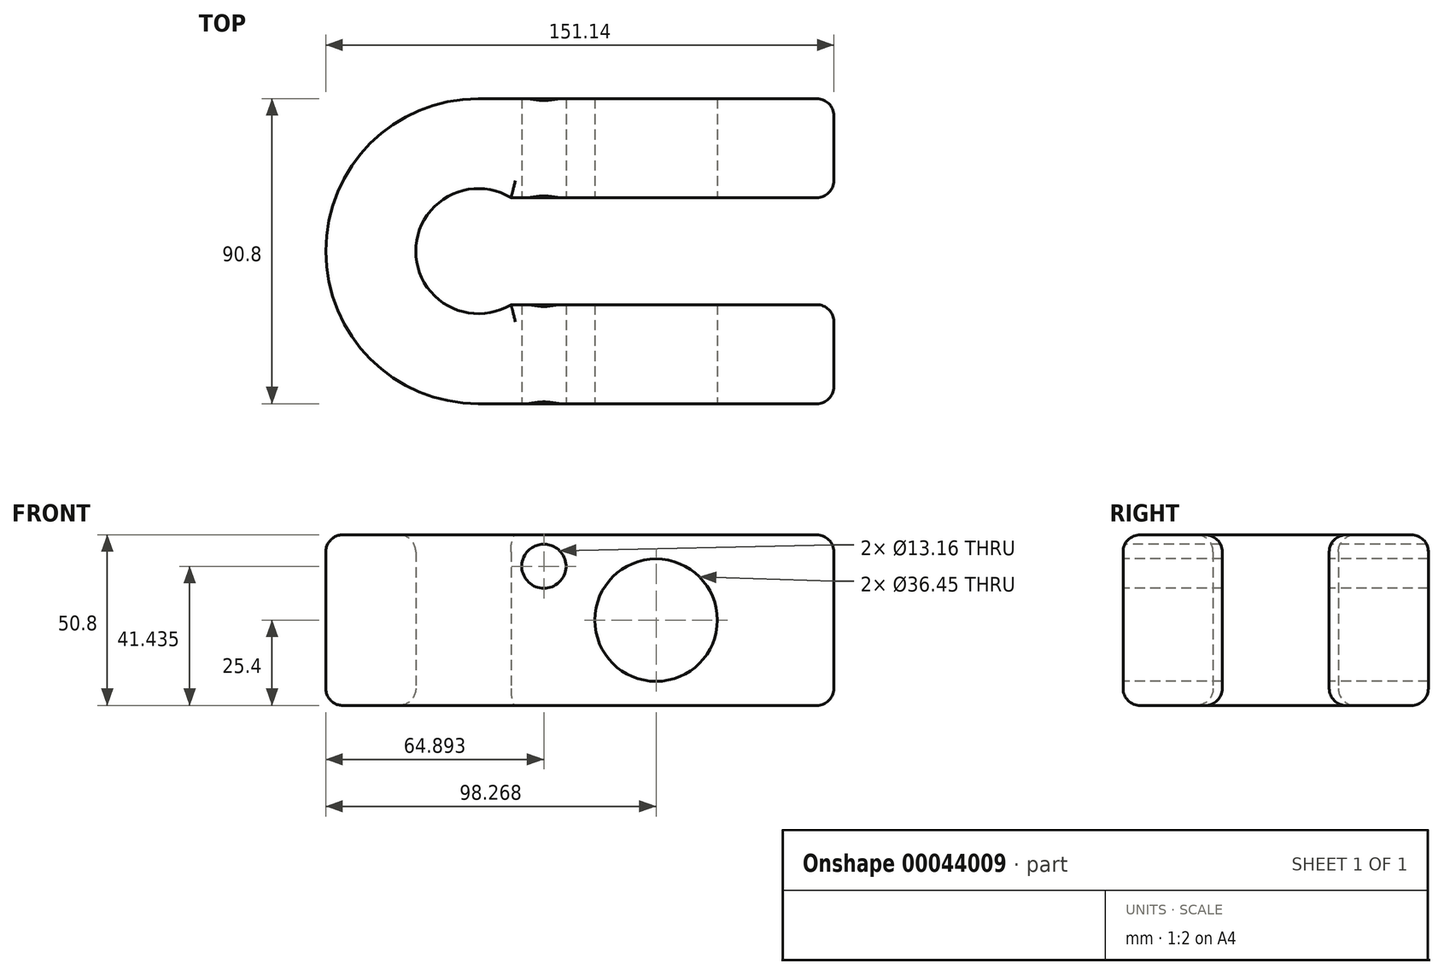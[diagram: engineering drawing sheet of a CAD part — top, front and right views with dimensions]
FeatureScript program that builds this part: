
annotation { "Feature Type Name" : "Feature", "Feature Type Description" : "" }
export const myFeature = defineFeature(function(context is Context, id is Id, definition is map)
    precondition{}
    {
        {
            var Q0;
            Q0=qCreatedBy(makeId("Top.planeOp"),FACE);
            var sketch = newSketch(context, id + "F0", { "sketchPlane" : qUnion([Q0])});
            skCircle(sketch, "E0", {"center": v(0, 0) * mm, "radius": 45.4 * mm});
            skLineSegment(sketch, "E1.bottom", {"start": v(0, 45.4) * mm, "end": v(105.74, 45.4) * mm});
            skLineSegment(sketch, "E1.top", {"start": v(0, -45.4) * mm, "end": v(105.74, -45.4) * mm});
            skLineSegment(sketch, "E1.left", {"start": v(0, 45.4) * mm, "end": v(0, -45.4) * mm});
            skLineSegment(sketch, "E1.right", {"start": v(105.74, 45.4) * mm, "end": v(105.74, -45.4) * mm});
            skCircle(sketch, "E2", {"center": v(0, 0) * mm, "radius": 18.62 * mm});
            skLineSegment(sketch, "E3.bottom", {"start": v(9.68, 15.9) * mm, "end": v(105.74, 15.9) * mm});
            skLineSegment(sketch, "E3.top", {"start": v(9.68, -15.9) * mm, "end": v(105.74, -15.9) * mm});
            skLineSegment(sketch, "E3.left", {"start": v(9.68, 15.9) * mm, "end": v(9.68, -15.9) * mm});
            skLineSegment(sketch, "E3.right", {"start": v(105.74, 15.9) * mm, "end": v(105.74, -15.9) * mm});
            skLineSegment(sketch, "E4", {"start": v(0, 0) * mm, "end": v(9.68, 0) * mm, "construction": true});
            skSolve(sketch);
        }
        {
            var Q0;
            {var subQ3=sQuery(id+"F0.wireOp",EDGE,"E1.bottom");Q0=makeQuery(id+"F0.imprint","IMPRINT",FACE,{"disambiguationData":[TD([[makeQuery(id+"F0.imprint","IMPRINT",EDGE,{"derivedFrom":subQ3}),-1.0]])]});}
            var Q1;
            {var subQ0=sQuery(id+"F0.wireOp",EDGE,"E3.bottom");var subQ1=sQuery(id+"F0.wireOp",EDGE,"E0");var subQ2=makeQuery(id+"F0.imprint","INTERSECT",VERTEX,{"derivedFrom":[subQ1,subQ0]});Q1=makeQuery(id+"F0.imprint","IMPRINT",FACE,{"disambiguationData":[TD([[makeQuery(id+"F0.imprint","IMPRINT",EDGE,{"disambiguationData":[TD([[subQ2,-1.0]])],"derivedFrom":subQ1}),1.0]])]});}
            var Q2;
            {var subQ0=sQuery(id+"F0.wireOp",EDGE,"E2");var subQ1=sQuery(id+"F0.wireOp",EDGE,"E1.left");var subQ3=makeQuery(id+"F0.imprint","INTERSECT",VERTEX,{"disambiguationData":[OD(0.0)],"derivedFrom":[subQ1,subQ0]});Q2=makeQuery(id+"F0.imprint","IMPRINT",FACE,{"disambiguationData":[TD([[makeQuery(id+"F0.imprint","IMPRINT",EDGE,{"disambiguationData":[TD([[subQ3,-1.0]])],"derivedFrom":subQ0}),-1.0]])]});}
            var Q3;
            {var subQ3=sQuery(id+"F0.wireOp",EDGE,"E1.top");Q3=makeQuery(id+"F0.imprint","IMPRINT",FACE,{"disambiguationData":[TD([[makeQuery(id+"F0.imprint","IMPRINT",EDGE,{"derivedFrom":subQ3}),1.0]])]});}
            var Q4;
            {var subQ3=sQuery(id+"F0.wireOp",EDGE,"E3.top");var subQ5=sQuery(id+"F0.wireOp",EDGE,"E0");var subQ7=makeQuery(id+"F0.imprint","INTERSECT",VERTEX,{"derivedFrom":[subQ5,subQ3]});Q4=makeQuery(id+"F0.imprint","IMPRINT",FACE,{"disambiguationData":[TD([[makeQuery(id+"F0.imprint","IMPRINT",EDGE,{"disambiguationData":[TD([[subQ7,1.0]])],"derivedFrom":subQ5}),1.0]])]});}
            extrude(context, id + "F1", {"entities" : qUnion([Q0, Q1, Q2, Q3, Q4]), "endBound" : BoundingType.SYMMETRIC, "depth" : 50.8 * mm});
        }
        {
            var Q0;
            Q0=makeQuery(id+"F1.opExtrude","SWEPT_FACE",FACE,{"disambiguationData":[OSD([sQuery(id+"F0.wireOp",EDGE,"E1.top")])]});
            var sketch = newSketch(context, id + "F2", { "sketchPlane" : qUnion([Q0])});
            skLineSegment(sketch, "E5", {"start": v(105.74, -25.4) * mm, "end": v(0, 25.4) * mm, "construction": true});
            skCircle(sketch, "E6", {"center": v(52.87, 0) * mm, "radius": 18.23 * mm});
            skCircle(sketch, "E7", {"center": v(19.5, 16.03) * mm, "radius": 6.58 * mm});
            skSolve(sketch);
        }
        {
            var Q0;
            Q0=makeQuery(id+"F2.imprint","IMPRINT",FACE,{"disambiguationData":[TD([[makeQuery(id+"F2.imprint","IMPRINT",EDGE,{"derivedFrom":sQuery(id+"F2.wireOp",EDGE,"E6")}),1.0]])]});
            var Q1;
            Q1=makeQuery(id+"F2.imprint","IMPRINT",FACE,{"disambiguationData":[TD([[makeQuery(id+"F2.imprint","IMPRINT",EDGE,{"derivedFrom":sQuery(id+"F2.wireOp",EDGE,"E7")}),1.0]])]});
            extrude(context, id + "F3", {"entities" : qUnion([Q0, Q1]), "operationType" : NewBodyOperationType.REMOVE, "endBound" : BoundingType.THROUGH_ALL, "oppositeDirection" : true, "depth" : 25.4 * mm});
        }
        {
            var Q0;
            Q0=makeQuery(id+"F1.opExtrude","CAP_FACE",FACE,{"disambiguationData":[OSD([sQuery(id+"F0.wireOp",EDGE,"E0"),sQuery(id+"F0.wireOp",EDGE,"E1.bottom"),sQuery(id+"F0.wireOp",EDGE,"E1.top"),sQuery(id+"F0.wireOp",EDGE,"E1.right"),sQuery(id+"F0.wireOp",EDGE,"E2"),sQuery(id+"F0.wireOp",EDGE,"E3.bottom"),sQuery(id+"F0.wireOp",EDGE,"E3.top")])],"isStart":false});
            var Q1;
            Q1=makeQuery(id+"F1.opExtrude","CAP_FACE",FACE,{"disambiguationData":[OSD([sQuery(id+"F0.wireOp",EDGE,"E0"),sQuery(id+"F0.wireOp",EDGE,"E1.bottom"),sQuery(id+"F0.wireOp",EDGE,"E1.top"),sQuery(id+"F0.wireOp",EDGE,"E1.right"),sQuery(id+"F0.wireOp",EDGE,"E2"),sQuery(id+"F0.wireOp",EDGE,"E3.bottom"),sQuery(id+"F0.wireOp",EDGE,"E3.top")])],"isStart":true});
            var Q2;
            {var subQ0=sQuery(id+"F0.wireOp",EDGE,"E1.right");Q2=makeQuery(id+"F1.opExtrude","SWEPT_FACE",FACE,{"disambiguationData":[OSD([subQ0]),TDD([makeQuery(id+"F0.imprint","IMPRINT",EDGE,{"disambiguationData":[TD([[makeQuery(id+"F0.imprint","INTERSECT",VERTEX,{"derivedFrom":[sQuery(id+"F0.wireOp",EDGE,"E1.top"),subQ0]}),1.0]])],"derivedFrom":subQ0})])]});}
            var Q3;
            {var subQ0=sQuery(id+"F0.wireOp",EDGE,"E1.right");Q3=makeQuery(id+"F1.opExtrude","SWEPT_FACE",FACE,{"disambiguationData":[OSD([subQ0]),TDD([makeQuery(id+"F0.imprint","IMPRINT",EDGE,{"disambiguationData":[TD([[makeQuery(id+"F0.imprint","INTERSECT",VERTEX,{"derivedFrom":[sQuery(id+"F0.wireOp",EDGE,"E1.bottom"),subQ0]}),-1.0]])],"derivedFrom":subQ0})])]});}
            fillet(context, id + "F4", {"entities" : qUnion([Q0, Q1, Q2, Q3]), "radius" : 5.08 * mm, "tangentPropagation" : true, "allowEdgeOverflow" : false});
        }
    });
